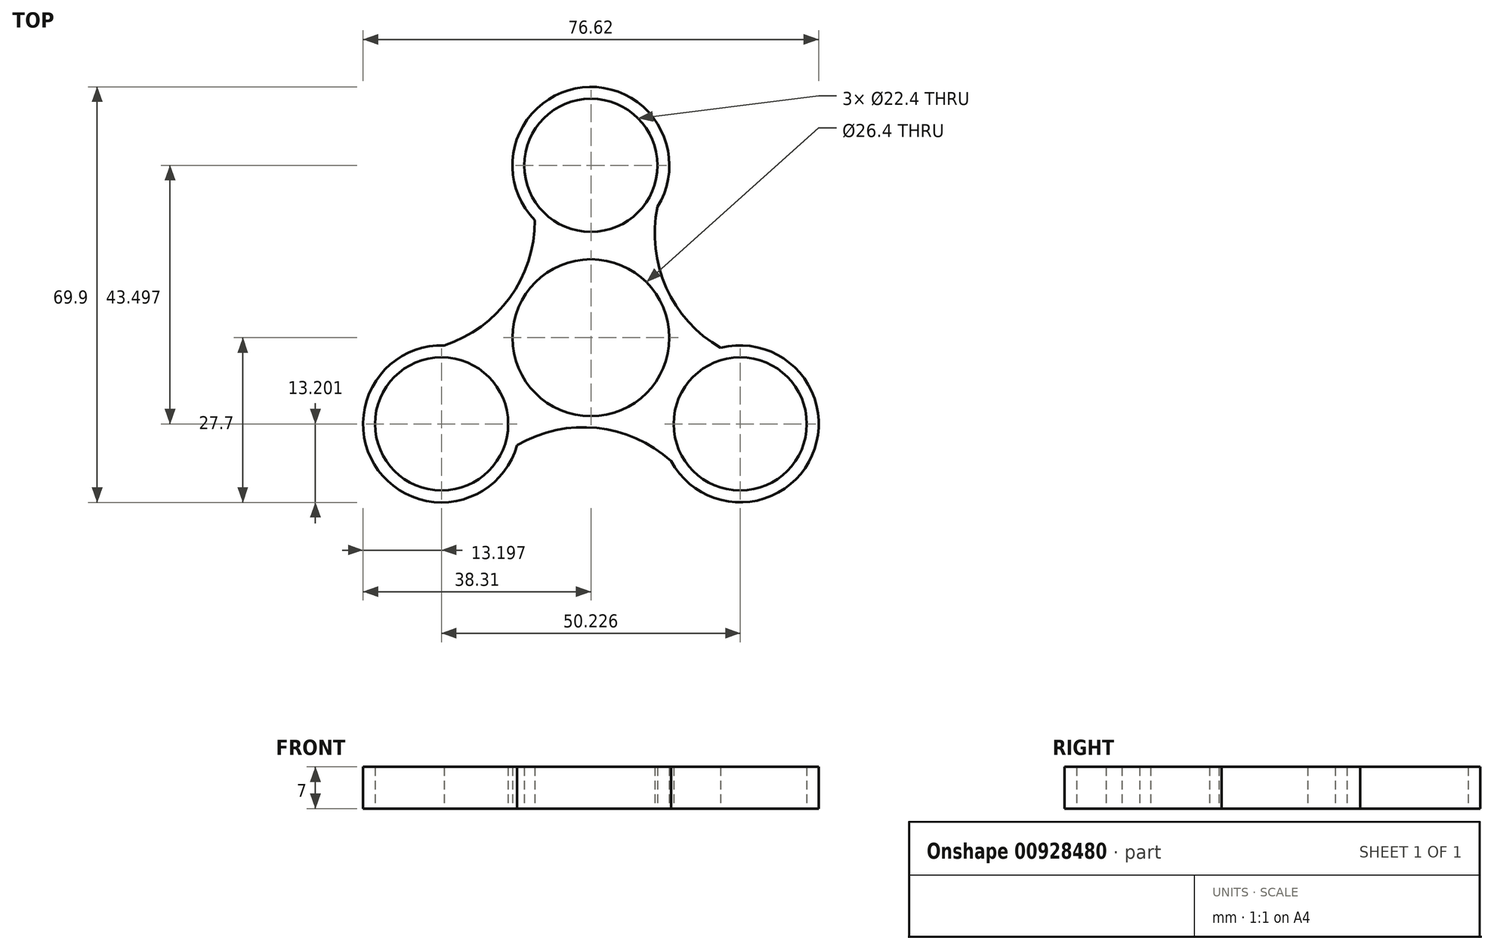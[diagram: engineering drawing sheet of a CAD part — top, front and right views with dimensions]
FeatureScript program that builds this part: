
annotation { "Feature Type Name" : "Feature", "Feature Type Description" : "" }
export const myFeature = defineFeature(function(context is Context, id is Id, definition is map)
    precondition{}
    {
        {
            var Q0;
            Q0=qCreatedBy(makeId("Top.planeOp"),FACE);
            var sketch = newSketch(context, id + "F0", { "sketchPlane" : qUnion([Q0])});
            skCircle(sketch, "E0", {"center": v(0, 0) * mm, "radius": 11.2 * mm});
            skCircle(sketch, "E1", {"center": v(0, 0) * mm, "radius": 13.2 * mm});
            skCircle(sketch, "E2", {"center": v(0, 29) * mm, "radius": 11.2 * mm});
            skArc(sketch, "E3", {"start": v(11.21, 22.03) * mm, "mid": v(-1.44, 42.12) * mm, "end": v(-9.43, 19.77) * mm});
            skArc(sketch, "E4.1.0", {"start": v(-24.69, -1.3) * mm, "mid": v(-35.76, -22.3) * mm, "end": v(-12.4, -18.05) * mm});
            skCircle(sketch, "E4.1.1", {"center": v(-25.11, -14.5) * mm, "radius": 11.2 * mm});
            skArc(sketch, "E4.2.0", {"start": v(13.47, -20.73) * mm, "mid": v(37.2, -19.81) * mm, "end": v(21.84, -1.71) * mm});
            skCircle(sketch, "E4.2.1", {"center": v(25.11, -14.5) * mm, "radius": 11.2 * mm});
            skArc(sketch, "E5", {"start": v(11.21, 22.03) * mm, "mid": v(12.66, 8.43) * mm, "end": v(21.84, -1.71) * mm});
            skArc(sketch, "E6.1.0", {"start": v(-24.69, -1.3) * mm, "mid": v(-13.63, 6.75) * mm, "end": v(-9.43, 19.77) * mm});
            skArc(sketch, "E6.2.0", {"start": v(13.47, -20.73) * mm, "mid": v(0.97, -15.18) * mm, "end": v(-12.4, -18.05) * mm});
            skSolve(sketch);
        }
        {
            var Q0;
            Q0 = qSketchRegion(id + "F0", true);
            extrude(context, id + "F1", {"entities" : qUnion([Q0]), "flatOperationType" : FlatOperationType.REMOVE, "depth" : 7 * mm, "offsetDistance" : 25 * mm, "domain" : OperationDomain.MODEL});
        }
    });
